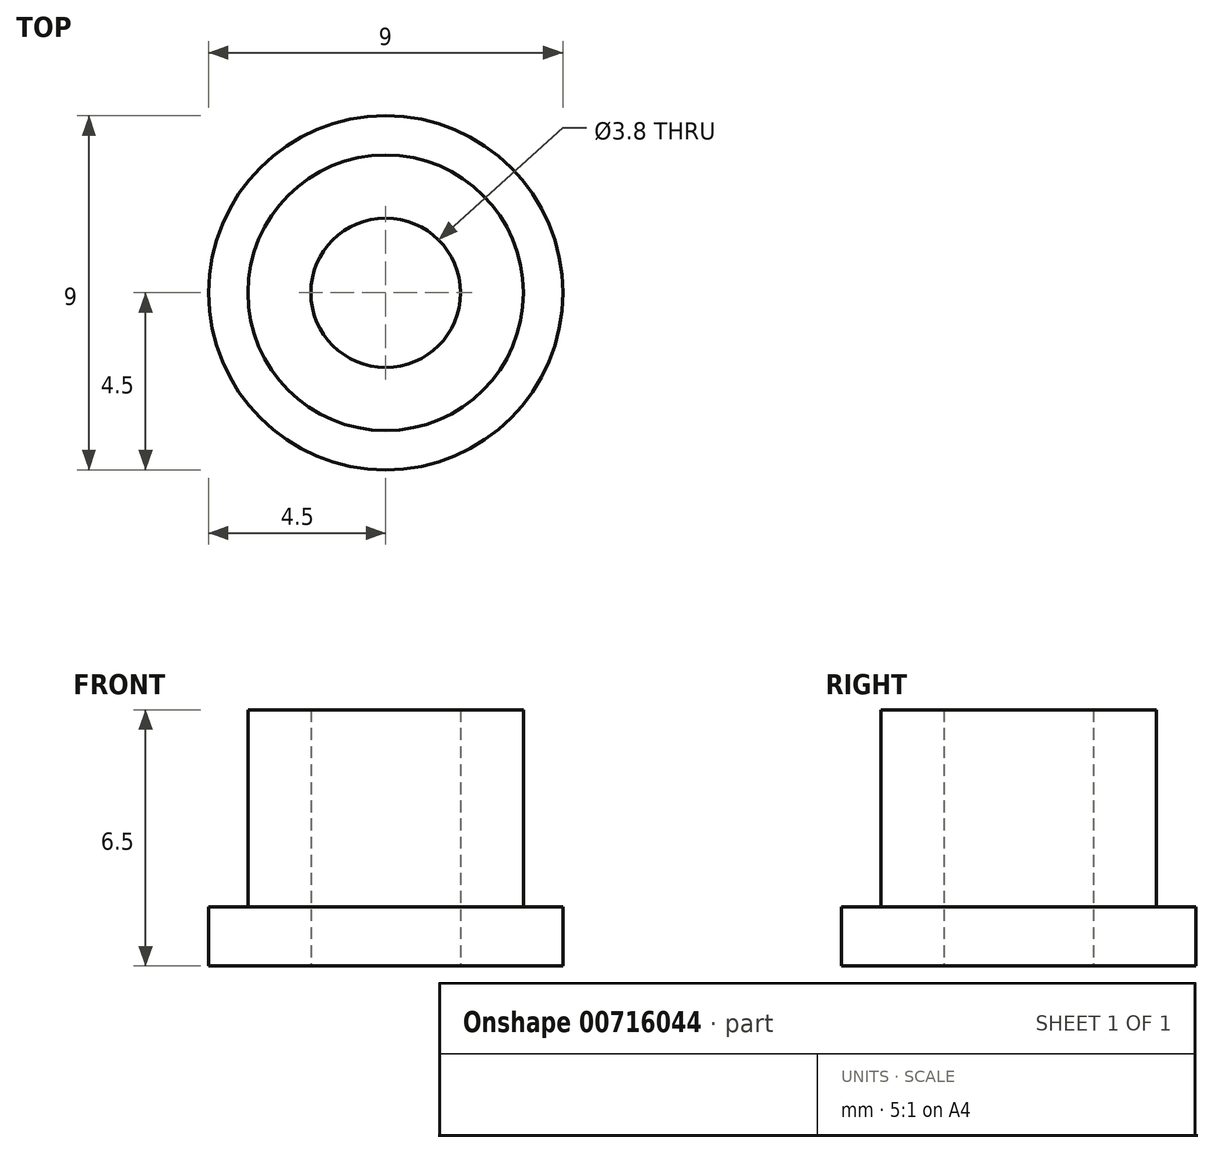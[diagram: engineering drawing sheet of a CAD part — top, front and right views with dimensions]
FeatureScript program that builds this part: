
annotation { "Feature Type Name" : "Feature", "Feature Type Description" : "" }
export const myFeature = defineFeature(function(context is Context, id is Id, definition is map)
    precondition{}
    {
        {
            var Q0;
            Q0=qCreatedBy(makeId("Top.planeOp"),FACE);
            var sketch = newSketch(context, id + "F0", { "sketchPlane" : qUnion([Q0])});
            skCircle(sketch, "E0", {"center": v(0, 0) * mm, "radius": 4.5 * mm});
            skSolve(sketch);
        }
        {
            var Q0;
            Q0=makeQuery(id+"F0.imprint","IMPRINT",FACE,{"disambiguationData":[TD([[makeQuery(id+"F0.imprint","IMPRINT",EDGE,{"derivedFrom":sQuery(id+"F0.wireOp",EDGE,"E0")}),1.0]])]});
            extrude(context, id + "F1", {"entities" : qUnion([Q0]), "depth" : 1.5 * mm, "offsetDistance" : 25 * mm});
        }
        {
            var Q0;
            Q0=makeQuery(id+"F1.opExtrude","CAP_FACE",FACE,{"disambiguationData":[OSD([sQuery(id+"F0.wireOp",EDGE,"E0")])],"isStart":false});
            var sketch = newSketch(context, id + "F2", { "sketchPlane" : qUnion([Q0])});
            skCircle(sketch, "E1", {"center": v(0, 0) * mm, "radius": 3.5 * mm});
            skSolve(sketch);
        }
        {
            var Q0;
            Q0 = qSketchRegion(id + "F2", true);
            extrude(context, id + "F3", {"entities" : qUnion([Q0]), "operationType" : NewBodyOperationType.ADD, "depth" : 5 * mm, "offsetDistance" : 25 * mm});
        }
        {
            var Q0;
            Q0=qCreatedBy(makeId("Top.planeOp"),FACE);
            var sketch = newSketch(context, id + "F4", { "sketchPlane" : qUnion([Q0])});
            skCircle(sketch, "E2", {"center": v(0, 0) * mm, "radius": 1.9 * mm});
            skSolve(sketch);
        }
        {
            var Q0;
            Q0 = qSketchRegion(id + "F4", true);
            extrude(context, id + "F5", {"entities" : qUnion([Q0]), "operationType" : NewBodyOperationType.REMOVE, "depth" : 25 * mm, "offsetDistance" : 25 * mm});
        }
    });
